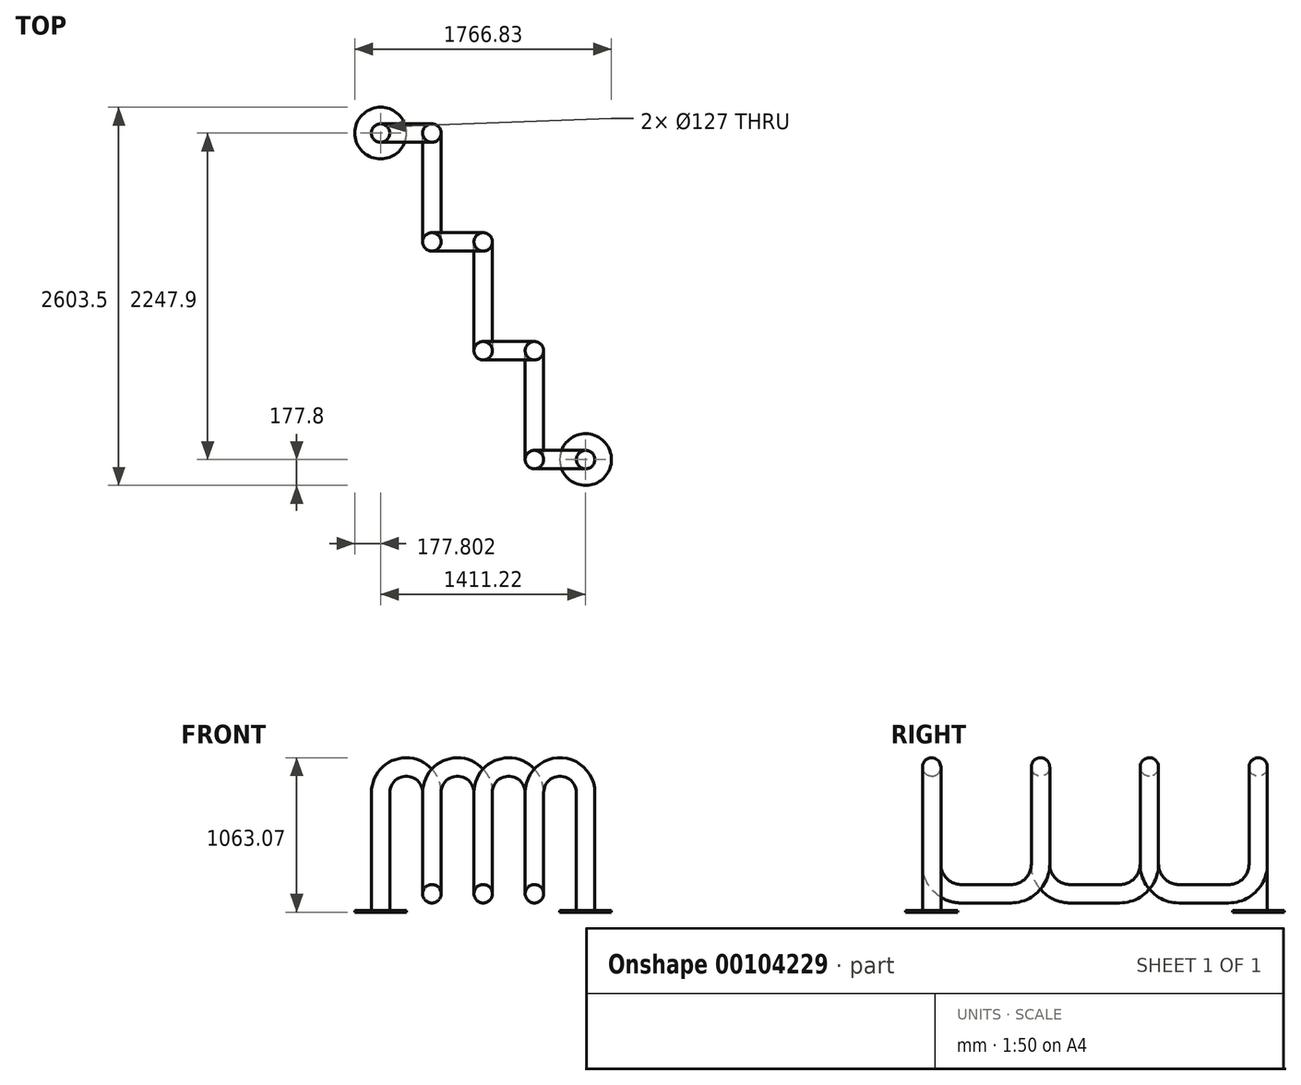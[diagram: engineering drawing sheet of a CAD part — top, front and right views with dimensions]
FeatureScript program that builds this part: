
annotation { "Feature Type Name" : "Feature", "Feature Type Description" : "" }
export const myFeature = defineFeature(function(context is Context, id is Id, definition is map)
    precondition{}
    {
        {
            var Q0;
            Q0=qCreatedBy(makeId("Front.planeOp"),FACE);
            var sketch = newSketch(context, id + "F0", { "sketchPlane" : qUnion([Q0])});
            skArc(sketch, "E0", {"start": v(352.8, 0) * mm, "mid": v(176.4, 176.4) * mm, "end": v(0, 0) * mm});
            skLineSegment(sketch, "E1", {"start": v(352.8, 0) * mm, "end": v(352.8, -810.47) * mm});
            skSolve(sketch);
        }
        {
            var Q0;
            Q0=qCreatedBy(makeId("Right.planeOp"),FACE);
            var sketch = newSketch(context, id + "F1", { "sketchPlane" : qUnion([Q0])});
            skLineSegment(sketch, "E2", {"start": v(0, 0) * mm, "end": v(0, -492.97) * mm});
            skLineSegment(sketch, "E3", {"start": v(749.3, -492.97) * mm, "end": v(749.3, 0) * mm});
            skLineSegment(sketch, "E4", {"start": v(203.2, -696.17) * mm, "end": v(546.1, -696.17) * mm});
            skPoint(sketch, "E5.visualSharp", {"position": v(0, -696.17) * mm});
            skArc(sketch, "E5.filletArc", {"start": v(0, -492.97) * mm, "mid": v(59.52, -636.66) * mm, "end": v(203.2, -696.17) * mm});
            skPoint(sketch, "E6.visualSharp", {"position": v(749.3, -696.17) * mm});
            skArc(sketch, "E6.filletArc", {"start": v(546.1, -696.17) * mm, "mid": v(689.78, -636.66) * mm, "end": v(749.3, -492.97) * mm});
            skSolve(sketch);
        }
        {
            var Q0;
            Q0=sQuery(id+"F1.wireOp",VERTEX,"E3.end");
            var Q1;
            Q1=qCreatedBy(makeId("Front.planeOp"),FACE);
            cPlane(context, id + "F2", {"entities" : qUnion([Q0, Q1]), "cplaneType" : CPlaneType.PLANE_POINT, "offset" : 152.4 * mm, "width" : 152.4 * mm, "height" : 152.4 * mm});
        }
        {
            var Q0;
            Q0=qCreatedBy(id+"F2.planeOp",FACE);
            var sketch = newSketch(context, id + "F3", { "sketchPlane" : qUnion([Q0])});
            skArc(sketch, "E7", {"start": v(0, 0) * mm, "mid": v(-176.4, 176.4) * mm, "end": v(-352.8, 0) * mm});
            skSolve(sketch);
        }
        {
            var Q0;
            Q0=qCreatedBy(makeId("Right.planeOp"),FACE);
            var Q1;
            Q1=sQuery(id+"F3.wireOp",VERTEX,"E7.end");
            cPlane(context, id + "F4", {"entities" : qUnion([Q0, Q1]), "cplaneType" : CPlaneType.PLANE_POINT, "offset" : 152.4 * mm, "width" : 152.4 * mm, "height" : 152.4 * mm});
        }
        {
            var Q0;
            Q0=qCreatedBy(id+"F4.planeOp",FACE);
            var sketch = newSketch(context, id + "F5", { "sketchPlane" : qUnion([Q0])});
            skLineSegment(sketch, "E8", {"start": v(1498.6, -492.97) * mm, "end": v(1498.6, 0) * mm});
            skLineSegment(sketch, "E9", {"start": v(952.5, -696.17) * mm, "end": v(1295.4, -696.17) * mm});
            skPoint(sketch, "E10.visualSharp", {"position": v(1498.6, -696.17) * mm});
            skArc(sketch, "E10.filletArc", {"start": v(1295.4, -696.17) * mm, "mid": v(1439.08, -636.66) * mm, "end": v(1498.6, -492.97) * mm});
            skLineSegment(sketch, "E11", {"start": v(749.3, -492.97) * mm, "end": v(749.3, 0) * mm});
            skPoint(sketch, "E12.visualSharp", {"position": v(749.3, -696.17) * mm});
            skArc(sketch, "E12.filletArc", {"start": v(749.3, -492.97) * mm, "mid": v(808.82, -636.66) * mm, "end": v(952.5, -696.17) * mm});
            skSolve(sketch);
        }
        {
            var Q0;
            Q0=qCreatedBy(id+"F2.planeOp",FACE);
            var Q1;
            Q1=sQuery(id+"F5.wireOp",VERTEX,"E8.end");
            cPlane(context, id + "F6", {"entities" : qUnion([Q0, Q1]), "cplaneType" : CPlaneType.PLANE_POINT, "offset" : 152.4 * mm, "width" : 152.4 * mm, "height" : 152.4 * mm});
        }
        {
            var Q0;
            Q0=qCreatedBy(id+"F6.planeOp",FACE);
            var sketch = newSketch(context, id + "F7", { "sketchPlane" : qUnion([Q0])});
            skArc(sketch, "E13", {"start": v(-352.8, 0) * mm, "mid": v(-529.2, 176.4) * mm, "end": v(-705.61, 0) * mm});
            skSolve(sketch);
        }
        {
            var Q0;
            Q0=qCreatedBy(id+"F4.planeOp",FACE);
            var Q1;
            Q1=sQuery(id+"F7.wireOp",VERTEX,"E13.end");
            cPlane(context, id + "F8", {"entities" : qUnion([Q0, Q1]), "cplaneType" : CPlaneType.PLANE_POINT, "offset" : 152.4 * mm, "width" : 152.4 * mm, "height" : 152.4 * mm});
        }
        {
            var Q0;
            Q0=qCreatedBy(id+"F8.planeOp",FACE);
            var sketch = newSketch(context, id + "F9", { "sketchPlane" : qUnion([Q0])});
            skLineSegment(sketch, "E14", {"start": v(1701.8, -696.17) * mm, "end": v(2044.7, -696.17) * mm});
            skLineSegment(sketch, "E15", {"start": v(2247.9, -492.97) * mm, "end": v(2247.9, 0) * mm});
            skPoint(sketch, "E16.visualSharp", {"position": v(2247.9, -696.17) * mm});
            skArc(sketch, "E16.filletArc", {"start": v(2044.7, -696.17) * mm, "mid": v(2188.38, -636.66) * mm, "end": v(2247.9, -492.97) * mm});
            skLineSegment(sketch, "E17", {"start": v(1498.6, 0) * mm, "end": v(1498.6, -492.97) * mm});
            skPoint(sketch, "E18.visualSharp", {"position": v(1498.6, -696.17) * mm});
            skArc(sketch, "E18.filletArc", {"start": v(1498.6, -492.97) * mm, "mid": v(1558.12, -636.66) * mm, "end": v(1701.8, -696.17) * mm});
            skSolve(sketch);
        }
        {
            var Q0;
            Q0=qCreatedBy(id+"F6.planeOp",FACE);
            var Q1;
            Q1=sQuery(id+"F9.wireOp",VERTEX,"E15.end");
            cPlane(context, id + "F10", {"entities" : qUnion([Q0, Q1]), "cplaneType" : CPlaneType.PLANE_POINT, "offset" : 152.4 * mm, "width" : 152.4 * mm, "height" : 152.4 * mm});
        }
        {
            var Q0;
            Q0=qCreatedBy(id+"F10.planeOp",FACE);
            var sketch = newSketch(context, id + "F11", { "sketchPlane" : qUnion([Q0])});
            skArc(sketch, "E19", {"start": v(-705.61, 0) * mm, "mid": v(-882.02, 176.4) * mm, "end": v(-1058.42, 0) * mm});
            skLineSegment(sketch, "E20", {"start": v(-1058.42, 0) * mm, "end": v(-1058.42, -810.47) * mm});
            skSolve(sketch);
        }
        {
            var Q0;
            Q0=qCreatedBy(makeId("Top.planeOp"),FACE);
            var sketch = newSketch(context, id + "F12", { "sketchPlane" : qUnion([Q0])});
            skCircle(sketch, "E21", {"center": v(0, 0) * mm, "radius": 63.5 * mm});
            skSolve(sketch);
        }
        {
            var Q0;
            Q0=makeQuery(id+"F12.imprint","IMPRINT",FACE,{"disambiguationData":[TD([[makeQuery(id+"F12.imprint","IMPRINT",EDGE,{"derivedFrom":sQuery(id+"F12.wireOp",EDGE,"E21")}),1.0]])]});
            var Q1;
            Q1=sQuery(id+"F1.wireOp",EDGE,"E2");
            var Q2;
            Q2=sQuery(id+"F1.wireOp",EDGE,"E5.filletArc");
            var Q3;
            Q3=sQuery(id+"F1.wireOp",EDGE,"E4");
            var Q4;
            Q4=sQuery(id+"F1.wireOp",EDGE,"E6.filletArc");
            var Q5;
            Q5=sQuery(id+"F1.wireOp",EDGE,"E3");
            var Q6;
            Q6=sQuery(id+"F3.wireOp",EDGE,"E7");
            var Q7;
            Q7=sQuery(id+"F5.wireOp",EDGE,"E11");
            var Q8;
            Q8=sQuery(id+"F5.wireOp",EDGE,"E12.filletArc");
            var Q9;
            Q9=sQuery(id+"F5.wireOp",EDGE,"E9");
            var Q10;
            Q10=sQuery(id+"F5.wireOp",EDGE,"E10.filletArc");
            var Q11;
            Q11=sQuery(id+"F5.wireOp",EDGE,"E8");
            var Q12;
            Q12=sQuery(id+"F7.wireOp",EDGE,"E13");
            var Q13;
            Q13=sQuery(id+"F9.wireOp",EDGE,"E17");
            var Q14;
            Q14=sQuery(id+"F9.wireOp",EDGE,"E18.filletArc");
            var Q15;
            Q15=sQuery(id+"F9.wireOp",EDGE,"E14");
            var Q16;
            Q16=sQuery(id+"F9.wireOp",EDGE,"E16.filletArc");
            var Q17;
            Q17=sQuery(id+"F9.wireOp",EDGE,"E15");
            var Q18;
            Q18=sQuery(id+"F11.wireOp",EDGE,"E19");
            var Q19;
            Q19=sQuery(id+"F11.wireOp",EDGE,"E20");
            sweep(context, id + "F13", {"profiles" : qUnion([Q0]), "path" : qUnion([Q1, Q2, Q3, Q4, Q5, Q6, Q7, Q8, Q9, Q10, Q11, Q12, Q13, Q14, Q15, Q16, Q17, Q18, Q19])});
        }
        {
            var Q0;
            Q0=makeQuery(id+"F13.opSweep","CAP_FACE",FACE,{"disambiguationData":[OSD([sQuery(id+"F1.wireOp",VERTEX,"E2.start"),sQuery(id+"F12.wireOp",EDGE,"E21")])],"isStart":true});
            var Q1;
            Q1=sQuery(id+"F0.wireOp",EDGE,"E0");
            var Q2;
            Q2=sQuery(id+"F0.wireOp",EDGE,"E1");
            sweep(context, id + "F14", {"operationType" : NewBodyOperationType.ADD, "profiles" : qUnion([Q0]), "path" : qUnion([Q1, Q2])});
        }
        {
            var Q0;
            Q0=makeQuery(id+"F14.opSweep","CAP_FACE",FACE,{"disambiguationData":[OSD([sQuery(id+"F0.wireOp",VERTEX,"E1.end"),sQuery(id+"F1.wireOp",VERTEX,"E2.start"),sQuery(id+"F12.wireOp",EDGE,"E21")])],"isStart":false});
            var sketch = newSketch(context, id + "F15", { "sketchPlane" : qUnion([Q0])});
            skCircle(sketch, "E22", {"center": v(352.8, 0) * mm, "radius": 177.8 * mm});
            skSolve(sketch);
        }
        {
            var Q0;
            Q0=makeQuery(id+"F15.imprint","IMPRINT",FACE,{"disambiguationData":[TD([[makeQuery(id+"F15.imprint","IMPRINT",EDGE,{"derivedFrom":sQuery(id+"F15.wireOp",EDGE,"E22")}),1.0]])]});
            extrude(context, id + "F16", {"entities" : qUnion([Q0]), "depth" : 12.7 * mm});
        }
        {
            var Q0;
            Q0=makeQuery(id+"F13.opSweep","CAP_FACE",FACE,{"disambiguationData":[OSD([sQuery(id+"F11.wireOp",VERTEX,"E20.end"),sQuery(id+"F12.wireOp",EDGE,"E21")])],"isStart":false});
            var sketch = newSketch(context, id + "F17", { "sketchPlane" : qUnion([Q0])});
            skCircle(sketch, "E23", {"center": v(-1058.42, -2247.9) * mm, "radius": 177.8 * mm});
            skSolve(sketch);
        }
        {
            var Q0;
            Q0=makeQuery(id+"F17.imprint","IMPRINT",FACE,{"disambiguationData":[TD([[makeQuery(id+"F17.imprint","IMPRINT",EDGE,{"derivedFrom":sQuery(id+"F17.wireOp",EDGE,"E23")}),1.0]])]});
            extrude(context, id + "F18", {"entities" : qUnion([Q0]), "depth" : 12.7 * mm});
        }
    });
